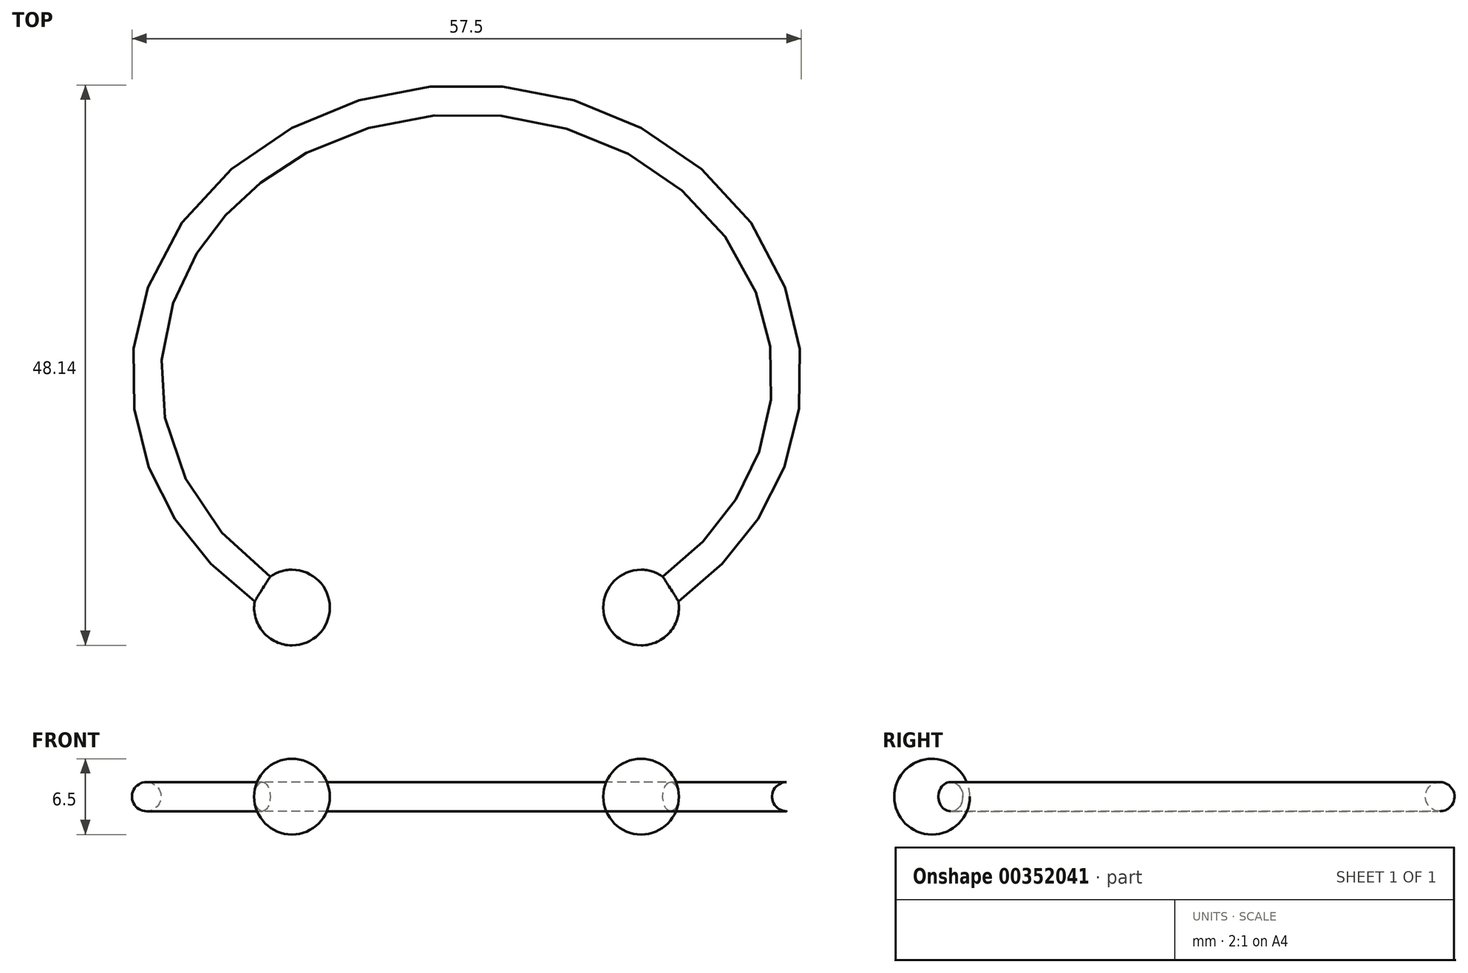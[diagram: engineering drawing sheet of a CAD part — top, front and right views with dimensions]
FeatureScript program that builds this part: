
annotation { "Feature Type Name" : "Feature", "Feature Type Description" : "" }
export const myFeature = defineFeature(function(context is Context, id is Id, definition is map)
    precondition{}
    {
        {
            var Q0;
            Q0=qCreatedBy(makeId("Top.planeOp"),FACE);
            var sketch = newSketch(context, id + "F0", { "sketchPlane" : qUnion([Q0])});
            skEllipse(sketch, "E0", {"center": v(0, 0) * mm, "majorRadius": 27.5 * mm, "minorRadius": 23.75 * mm, "majorAxis": v(-1, 0)});
            skSolve(sketch);
        }
        {
            var Q0;
            Q0=qCreatedBy(makeId("Front.planeOp"),FACE);
            var sketch = newSketch(context, id + "F1", { "sketchPlane" : qUnion([Q0])});
            skLineSegment(sketch, "E1", {"start": v(0, 0) * mm, "end": v(0, 2.45) * mm, "construction": true});
            skCircle(sketch, "E2", {"center": v(27.5, 0) * mm, "radius": 1.25 * mm});
            skSolve(sketch);
        }
        {
            var Q0;
            Q0=makeQuery(id+"F1.imprint","IMPRINT",FACE,{"disambiguationData":[TD([[makeQuery(id+"F1.imprint","IMPRINT",EDGE,{"derivedFrom":sQuery(id+"F1.wireOp",EDGE,"E2")}),1.0]])]});
            var Q1;
            Q1=sQuery(id+"F0.wireOp",EDGE,"E0");
            sweep(context, id + "F2", {"profiles" : qUnion([Q0]), "path" : qUnion([Q1])});
        }
        {
            var Q0;
            Q0=qCreatedBy(makeId("Top.planeOp"),FACE);
            var sketch = newSketch(context, id + "F3", { "sketchPlane" : qUnion([Q0])});
            skLineSegment(sketch, "E3.bottom", {"start": v(15, 0) * mm, "end": v(-15, 0) * mm});
            skLineSegment(sketch, "E3.top", {"start": v(15, -30) * mm, "end": v(-15, -30) * mm});
            skLineSegment(sketch, "E3.left", {"start": v(15, 0) * mm, "end": v(15, -30) * mm});
            skLineSegment(sketch, "E3.right", {"start": v(-15, 0) * mm, "end": v(-15, -30) * mm});
            skPoint(sketch, "E3.middle", {"position": v(0, -15) * mm});
            skSolve(sketch);
        }
        {
            var Q0;
            Q0=makeQuery(id+"F3.imprint","IMPRINT",FACE,{"disambiguationData":[TD([[makeQuery(id+"F3.imprint","IMPRINT",EDGE,{"derivedFrom":sQuery(id+"F3.wireOp",EDGE,"E3.bottom")}),1.0]])]});
            extrude(context, id + "F4", {"entities" : qUnion([Q0]), "operationType" : NewBodyOperationType.REMOVE, "endBound" : BoundingType.SYMMETRIC, "oppositeDirection" : true, "depth" : 25 * mm});
        }
        {
            var Q0;
            Q0=makeQuery(id+"F4.boolean.opBoolean","COPY",FACE,{"derivedFrom":makeQuery(id+"F4.opExtrude","SWEPT_FACE",FACE,{"disambiguationData":[OSD([sQuery(id+"F3.wireOp",EDGE,"E3.right")])]})});
            var sketch = newSketch(context, id + "F5", { "sketchPlane" : qUnion([Q0])});
            skArc(sketch, "E4", {"start": v(-16.64, 0) * mm, "mid": v(-19.9, 3.25) * mm, "end": v(-23.14, 0) * mm});
            skLineSegment(sketch, "E5", {"start": v(-21.33, 0) * mm, "end": v(-18.46, 0) * mm, "construction": true});
            skLineSegment(sketch, "E6", {"start": v(-23.14, 0) * mm, "end": v(-16.64, 0) * mm});
            skSolve(sketch);
        }
        {
            var Q0;
            Q0 = qSketchRegion(id + "F5", true);
            var Q1;
            Q1=sQuery(id+"F5.wireOp",EDGE,"E4");
            var Q2;
            Q2=sQuery(id+"F5.wireOp",EDGE,"E6");
            revolve(context, id + "F6", {"operationType" : NewBodyOperationType.ADD, "entities" : qUnion([Q0]), "surfaceEntities" : qUnion([Q1]), "axis" : qUnion([Q2]), "revolveType" : RevolveType.FULL});
        }
        {
            var Q0;
            Q0=makeQuery(id+"F4.boolean.opBoolean","COPY",FACE,{"derivedFrom":makeQuery(id+"F4.opExtrude","SWEPT_FACE",FACE,{"disambiguationData":[OSD([sQuery(id+"F3.wireOp",EDGE,"E3.left")])]})});
            var sketch = newSketch(context, id + "F7", { "sketchPlane" : qUnion([Q0])});
            skLineSegment(sketch, "E7", {"start": v(21.33, 0) * mm, "end": v(18.46, 0) * mm, "construction": true});
            skArc(sketch, "E8", {"start": v(16.64, 0) * mm, "mid": v(19.9, -3.25) * mm, "end": v(23.14, 0) * mm});
            skPoint(sketch, "E8.startSnap0", {"position": v(19.9, 0) * mm});
            skLineSegment(sketch, "E9", {"start": v(23.14, 0) * mm, "end": v(16.64, 0) * mm});
            skSolve(sketch);
        }
        {
            var Q0;
            Q0 = qSketchRegion(id + "F7", true);
            var Q1;
            Q1=sQuery(id+"F7.wireOp",EDGE,"E8");
            var Q2;
            Q2=sQuery(id+"F7.wireOp",EDGE,"E9");
            revolve(context, id + "F8", {"operationType" : NewBodyOperationType.ADD, "entities" : qUnion([Q0]), "surfaceEntities" : qUnion([Q1]), "axis" : qUnion([Q2]), "revolveType" : RevolveType.FULL});
        }
    });
